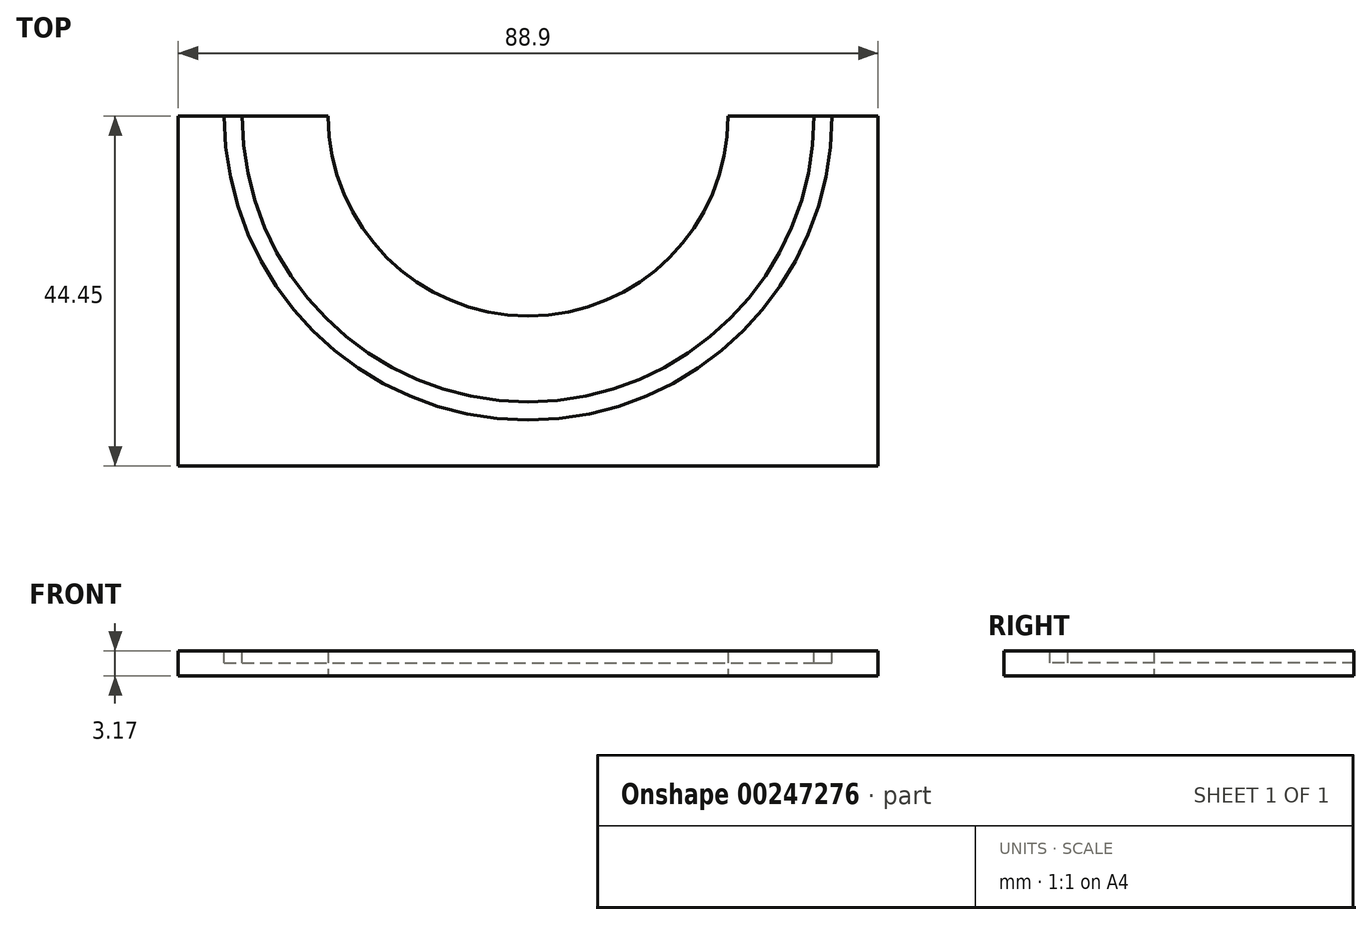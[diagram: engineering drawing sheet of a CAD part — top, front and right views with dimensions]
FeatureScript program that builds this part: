
annotation { "Feature Type Name" : "Feature", "Feature Type Description" : "" }
export const myFeature = defineFeature(function(context is Context, id is Id, definition is map)
    precondition{}
    {
        {
            var Q0;
            Q0=qCreatedBy(makeId("Top.planeOp"),FACE);
            var sketch = newSketch(context, id + "F0", { "sketchPlane" : qUnion([Q0])});
            skCircle(sketch, "E0", {"center": v(0, 0) * mm, "radius": 44.45 * mm, "construction": true});
            skLineSegment(sketch, "E1.bottom", {"start": v(-44.45, 0) * mm, "end": v(44.45, 0) * mm});
            skLineSegment(sketch, "E1.top", {"start": v(-44.45, -44.45) * mm, "end": v(44.45, -44.45) * mm});
            skLineSegment(sketch, "E1.left", {"start": v(-44.45, 0) * mm, "end": v(-44.45, -44.45) * mm});
            skLineSegment(sketch, "E1.right", {"start": v(44.45, 0) * mm, "end": v(44.45, -44.45) * mm});
            skSolve(sketch);
        }
        {
            var Q0;
            Q0=qSketchRegion(id+"F0",true);
            extrude(context, id + "F1", {"entities" : qUnion([Q0]), "depth" : 3.17 * mm});
        }
        {
            var Q0;
            Q0=makeQuery(id+"F1.opExtrude","CAP_FACE",FACE,{"disambiguationData":[OSD([sQuery(id+"F0.wireOp",EDGE,"E1.bottom"),sQuery(id+"F0.wireOp",EDGE,"E1.top"),sQuery(id+"F0.wireOp",EDGE,"E1.left"),sQuery(id+"F0.wireOp",EDGE,"E1.right")])],"isStart":false});
            var sketch = newSketch(context, id + "F2", { "sketchPlane" : qUnion([Q0])});
            skCircle(sketch, "E2", {"center": v(0, 0) * mm, "radius": 38.6 * mm});
            skCircle(sketch, "E3", {"center": v(0, 0) * mm, "radius": 36.32 * mm});
            skCircle(sketch, "E4", {"center": v(0, 0) * mm, "radius": 13.2 * mm});
            skSolve(sketch);
        }
        {
            var Q0;
            Q0=qSketchRegion(id+"F2",true);
            var Q1;
            Q1=makeQuery(id+"F2.imprint","IMPRINT",FACE,{"disambiguationData":[TD([[makeQuery(id+"F2.imprint","IMPRINT",EDGE,{"derivedFrom":sQuery(id+"F2.wireOp",EDGE,"E4")}),1.0]])]});
            extrude(context, id + "F3", {"entities" : qUnion([Q0, Q1]), "operationType" : NewBodyOperationType.REMOVE, "oppositeDirection" : true, "depth" : 1.52 * mm});
        }
        {
            var Q0;
            Q0=qCreatedBy(makeId("Top.planeOp"),FACE);
            var sketch = newSketch(context, id + "F4", { "sketchPlane" : qUnion([Q0])});
            skLineSegment(sketch, "E5", {"start": v(-44.45, 0) * mm, "end": v(44.45, 0) * mm});
            skCircle(sketch, "E6", {"center": v(0, 0) * mm, "radius": 25.4 * mm});
            skSolve(sketch);
        }
        {
            var Q0;
            Q0=qSketchRegion(id+"F4",true);
            extrude(context, id + "F5", {"entities" : qUnion([Q0]), "operationType" : NewBodyOperationType.REMOVE, "endBound" : BoundingType.THROUGH_ALL, "depth" : 25.4 * mm});
        }
    });
